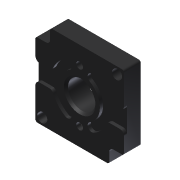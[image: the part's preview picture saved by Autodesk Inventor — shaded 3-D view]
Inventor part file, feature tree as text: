
AUTODESK INVENTOR PART (.ipt)
format: ipt  version: 2013 (Build 170138000, 138)  size: 279,040 bytes
history: native  units: in
note: dims shown in document units (in); Inventor stores cm internally (conversion verified against a paired STEP export)
features: fillet x1, other x1, imported_body x1
ambient origin geometry x8: Origin, YZ Plane, XZ Plane, XY Plane, X Axis, Y Axis, Z Axis, Center Point
feature tree (3):
  fillet  "Fillet4"  [1 undecoded]
  other  "217-2822-AM-9015 Mounting Plate STEP1"
  imported_body  "Base1"
note: 1 required parameter value undecoded (feature->parameter linkage not recoverable at this tier; creation-order binding heuristic only, values carry confidence <= 0.55)
